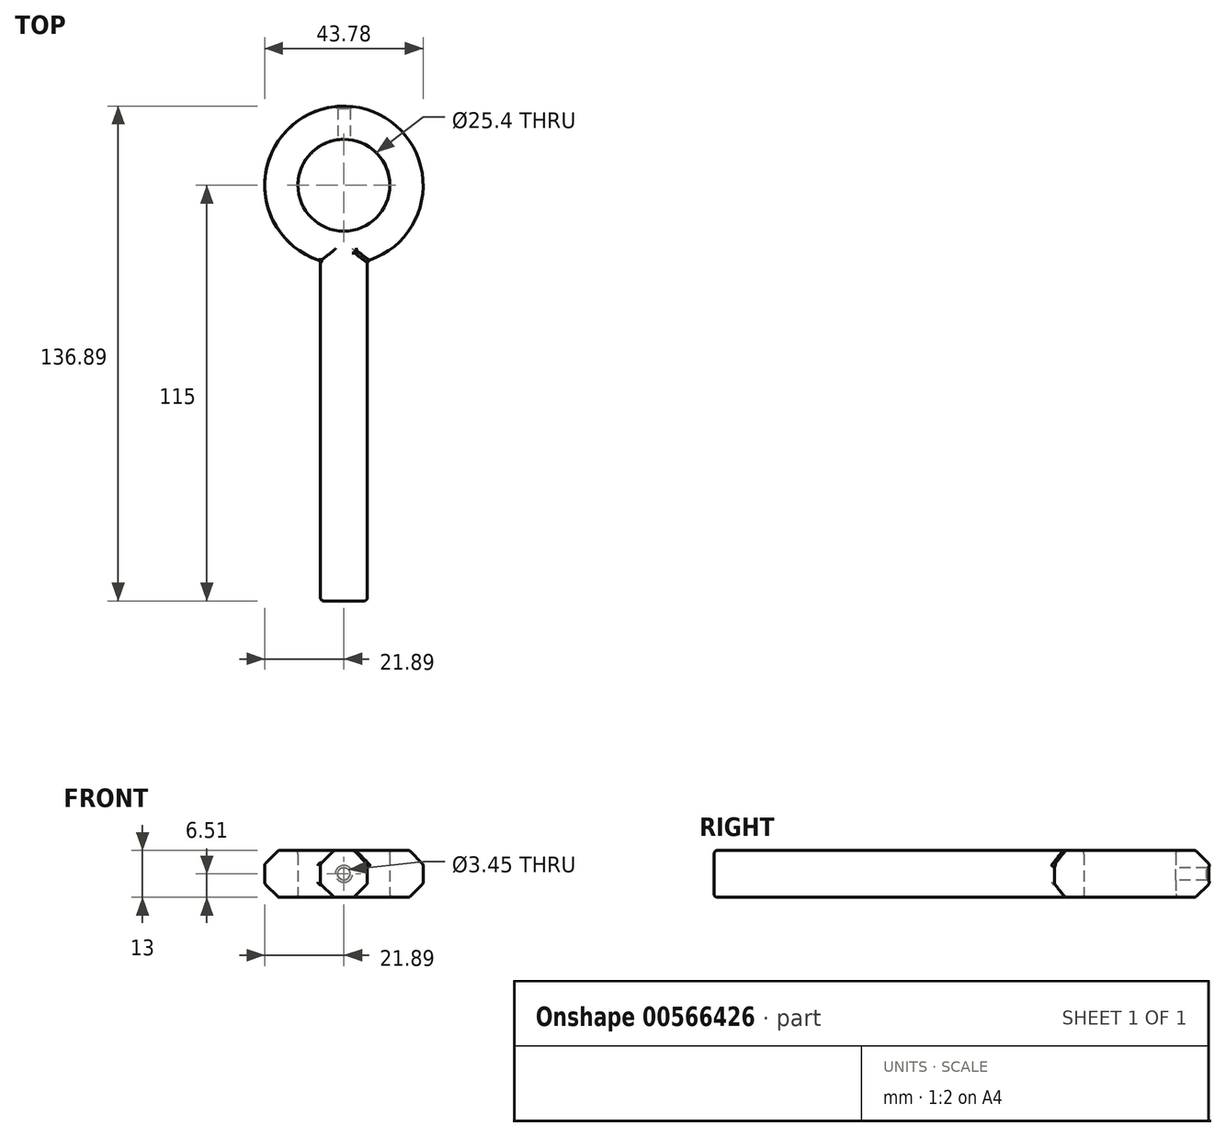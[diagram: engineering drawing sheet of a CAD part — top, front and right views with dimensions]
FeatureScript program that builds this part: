
annotation { "Feature Type Name" : "Feature", "Feature Type Description" : "" }
export const myFeature = defineFeature(function(context is Context, id is Id, definition is map)
    precondition{}
    {
        {
            var Q0;
            Q0=qCreatedBy(makeId("Right.planeOp"),FACE);
            var sketch = newSketch(context, id + "F0", { "sketchPlane" : qUnion([Q0])});
            skLineSegment(sketch, "E0", {"start": v(-12.7, 6.49) * mm, "end": v(-18.08, 6.49) * mm});
            skLineSegment(sketch, "E1", {"start": v(-18.08, 6.49) * mm, "end": v(-21.9, 2.68) * mm});
            skLineSegment(sketch, "E2", {"start": v(-21.9, 2.68) * mm, "end": v(-21.9, -2.7) * mm});
            skLineSegment(sketch, "E3", {"start": v(-21.9, -2.7) * mm, "end": v(-18.08, -6.51) * mm});
            skLineSegment(sketch, "E4", {"start": v(-18.08, -6.51) * mm, "end": v(-12.7, -6.51) * mm});
            skLineSegment(sketch, "E5", {"start": v(-12.7, 6.49) * mm, "end": v(-12.7, -6.51) * mm});
            skLineSegment(sketch, "E6", {"start": v(0, 0) * mm, "end": v(0, 10.16) * mm, "construction": true});
            skSolve(sketch);
        }
        {
            var Q0;
            Q0=makeQuery(id+"F0.imprint","IMPRINT",FACE,{"disambiguationData":[TD([[makeQuery(id+"F0.imprint","IMPRINT",EDGE,{"derivedFrom":sQuery(id+"F0.wireOp",EDGE,"E0")}),1.0]])]});
            var Q1;
            Q1=sQuery(id+"F0.wireOp",EDGE,"E6");
            revolve(context, id + "F1", {"entities" : qUnion([Q0]), "axis" : qUnion([Q1]), "revolveType" : RevolveType.FULL});
        }
        {
            var Q0;
            Q0=makeQuery(id+"F1.opRevolve","SWEPT_EDGE",EDGE,{"disambiguationData":[OSD([sQuery(id+"F0.wireOp",EDGE,"E0"),sQuery(id+"F0.wireOp",EDGE,"E5")])]});
            var Q1;
            Q1=makeQuery(id+"F1.opRevolve","SWEPT_EDGE",EDGE,{"disambiguationData":[OSD([sQuery(id+"F0.wireOp",EDGE,"E4"),sQuery(id+"F0.wireOp",EDGE,"E5")])]});
            fillet(context, id + "F2", {"entities" : qUnion([Q0, Q1]), "radius" : 1 * mm, "tangentPropagation" : true, "allowEdgeOverflow" : false});
        }
        {
            var Q0;
            Q0=makeQuery(id+"F1.opRevolve","SWEPT_EDGE",EDGE,{"disambiguationData":[OSD([sQuery(id+"F0.wireOp",EDGE,"E1"),sQuery(id+"F0.wireOp",EDGE,"E2")])]});
            var Q1;
            Q1=makeQuery(id+"F1.opRevolve","SWEPT_EDGE",EDGE,{"disambiguationData":[OSD([sQuery(id+"F0.wireOp",EDGE,"E0"),sQuery(id+"F0.wireOp",EDGE,"E1")])]});
            var Q2;
            Q2=makeQuery(id+"F1.opRevolve","SWEPT_EDGE",EDGE,{"disambiguationData":[OSD([sQuery(id+"F0.wireOp",EDGE,"E2"),sQuery(id+"F0.wireOp",EDGE,"E3")])]});
            var Q3;
            Q3=makeQuery(id+"F1.opRevolve","SWEPT_EDGE",EDGE,{"disambiguationData":[OSD([sQuery(id+"F0.wireOp",EDGE,"E3"),sQuery(id+"F0.wireOp",EDGE,"E4")])]});
            fillet(context, id + "F3", {"entities" : qUnion([Q0, Q1, Q2, Q3]), "radius" : 1 * mm, "tangentPropagation" : true, "allowEdgeOverflow" : false});
        }
        {
            var Q0;
            Q0=qCreatedBy(makeId("Front.planeOp"),FACE);
            var sketch = newSketch(context, id + "F4", { "sketchPlane" : qUnion([Q0])});
            skCircle(sketch, "E7", {"center": v(0, 0) * mm, "radius": 1.73 * mm});
            skSolve(sketch);
        }
        {
            var Q0;
            Q0 = qSketchRegion(id + "F4", true);
            extrude(context, id + "F5", {"entities" : qUnion([Q0]), "operationType" : NewBodyOperationType.REMOVE, "oppositeDirection" : true, "depth" : 25 * mm, "offsetDistance" : 25 * mm});
        }
        {
            var Q0;
            Q0=qCreatedBy(makeId("Front.planeOp"),FACE);
            var sketch = newSketch(context, id + "F6", { "sketchPlane" : qUnion([Q0])});
            skLineSegment(sketch, "E8", {"start": v(-6.5, 2.68) * mm, "end": v(-6.5, -2.7) * mm});
            skLineSegment(sketch, "E9", {"start": v(-6.5, -2.7) * mm, "end": v(-2.7, -6.51) * mm});
            skLineSegment(sketch, "E10", {"start": v(-2.7, -6.51) * mm, "end": v(2.7, -6.51) * mm});
            skLineSegment(sketch, "E11", {"start": v(2.7, -6.51) * mm, "end": v(6.5, -2.7) * mm});
            skLineSegment(sketch, "E12", {"start": v(6.5, -2.7) * mm, "end": v(6.5, 2.68) * mm});
            skLineSegment(sketch, "E13", {"start": v(6.5, 2.68) * mm, "end": v(2.7, 6.49) * mm});
            skLineSegment(sketch, "E14", {"start": v(2.7, 6.49) * mm, "end": v(-2.7, 6.49) * mm});
            skLineSegment(sketch, "E15", {"start": v(-2.7, 6.49) * mm, "end": v(-6.5, 2.68) * mm});
            skSolve(sketch);
        }
        {
            var Q0;
            Q0=makeQuery(id+"F6.imprint","IMPRINT",FACE,{"disambiguationData":[TD([[makeQuery(id+"F6.imprint","IMPRINT",EDGE,{"derivedFrom":sQuery(id+"F6.wireOp",EDGE,"E8")}),1.0]])]});
            extrude(context, id + "F7", {"entities" : qUnion([Q0]), "operationType" : NewBodyOperationType.ADD, "depth" : 115 * mm, "offsetDistance" : 25 * mm, "hasSecondDirection" : true, "secondDirectionOppositeDirection" : false, "secondDirectionDepth" : 15 * mm});
        }
        {
            var Q0;
            Q0=makeQuery(id+"F7.opExtrude","SWEPT_EDGE",EDGE,{"disambiguationData":[OSD([sQuery(id+"F6.wireOp",EDGE,"E14"),sQuery(id+"F6.wireOp",EDGE,"E15")])]});
            var Q1;
            Q1=makeQuery(id+"F7.opExtrude","SWEPT_EDGE",EDGE,{"disambiguationData":[OSD([sQuery(id+"F6.wireOp",EDGE,"E13"),sQuery(id+"F6.wireOp",EDGE,"E14")])]});
            var Q2;
            Q2=makeQuery(id+"F7.opExtrude","SWEPT_EDGE",EDGE,{"disambiguationData":[OSD([sQuery(id+"F6.wireOp",EDGE,"E8"),sQuery(id+"F6.wireOp",EDGE,"E15")])]});
            var Q3;
            Q3=makeQuery(id+"F7.opExtrude","SWEPT_FACE",FACE,{"disambiguationData":[OSD([sQuery(id+"F6.wireOp",EDGE,"E8")])]});
            var Q4;
            Q4=makeQuery(id+"F7.opExtrude","SWEPT_EDGE",EDGE,{"disambiguationData":[OSD([sQuery(id+"F6.wireOp",EDGE,"E9"),sQuery(id+"F6.wireOp",EDGE,"E10")])]});
            var Q5;
            Q5=makeQuery(id+"F7.opExtrude","SWEPT_EDGE",EDGE,{"disambiguationData":[OSD([sQuery(id+"F6.wireOp",EDGE,"E12"),sQuery(id+"F6.wireOp",EDGE,"E13")])]});
            var Q6;
            Q6=makeQuery(id+"F7.opExtrude","SWEPT_EDGE",EDGE,{"disambiguationData":[OSD([sQuery(id+"F6.wireOp",EDGE,"E11"),sQuery(id+"F6.wireOp",EDGE,"E12")])]});
            var Q7;
            Q7=makeQuery(id+"F7.opExtrude","SWEPT_EDGE",EDGE,{"disambiguationData":[OSD([sQuery(id+"F6.wireOp",EDGE,"E10"),sQuery(id+"F6.wireOp",EDGE,"E11")])]});
            var Q8;
            Q8=makeQuery(id+"F7.boolean.opBoolean","INTERSECT",EDGE,{"derivedFrom":[makeQuery(id+"F1.opRevolve","SWEPT_FACE",FACE,{"disambiguationData":[OSD([sQuery(id+"F0.wireOp",EDGE,"E1")])]}),makeQuery(id+"F7.opExtrude","SWEPT_FACE",FACE,{"disambiguationData":[OSD([sQuery(id+"F6.wireOp",EDGE,"E13")])]})]});
            var Q9;
            Q9=makeQuery(id+"F7.opExtrude","CAP_EDGE",EDGE,{"disambiguationData":[OSD([sQuery(id+"F6.wireOp",EDGE,"E15")])],"isStart":false});
            var Q10;
            Q10=makeQuery(id+"F7.opExtrude","CAP_EDGE",EDGE,{"disambiguationData":[OSD([sQuery(id+"F6.wireOp",EDGE,"E14")])],"isStart":false});
            var Q11;
            Q11=makeQuery(id+"F7.opExtrude","CAP_EDGE",EDGE,{"disambiguationData":[OSD([sQuery(id+"F6.wireOp",EDGE,"E13")])],"isStart":false});
            var Q12;
            Q12=makeQuery(id+"F7.opExtrude","CAP_EDGE",EDGE,{"disambiguationData":[OSD([sQuery(id+"F6.wireOp",EDGE,"E12")])],"isStart":false});
            var Q13;
            Q13=makeQuery(id+"F7.opExtrude","CAP_EDGE",EDGE,{"disambiguationData":[OSD([sQuery(id+"F6.wireOp",EDGE,"E11")])],"isStart":false});
            var Q14;
            Q14=makeQuery(id+"F7.opExtrude","CAP_EDGE",EDGE,{"disambiguationData":[OSD([sQuery(id+"F6.wireOp",EDGE,"E10")])],"isStart":false});
            var Q15;
            Q15=makeQuery(id+"F7.opExtrude","CAP_EDGE",EDGE,{"disambiguationData":[OSD([sQuery(id+"F6.wireOp",EDGE,"E9")])],"isStart":false});
            fillet(context, id + "F8", {"entities" : qUnion([Q0, Q1, Q2, Q3, Q4, Q5, Q6, Q7, Q8, Q9, Q10, Q11, Q12, Q13, Q14, Q15]), "radius" : 1 * mm, "tangentPropagation" : true, "allowEdgeOverflow" : false});
        }
        {
            var Q0;
            Q0=makeQuery(id+"F5.boolean.opBoolean","INTERSECT",EDGE,{"derivedFrom":[makeQuery(id+"F1.opRevolve","SWEPT_FACE",FACE,{"disambiguationData":[OSD([sQuery(id+"F0.wireOp",EDGE,"E2")])]}),makeQuery(id+"F5.opExtrude","SWEPT_FACE",FACE,{"disambiguationData":[OSD([sQuery(id+"F4.wireOp",EDGE,"E7")])]})]});
            chamfer(context, id + "F9", {"entities" : qUnion([Q0]), "width" : .6 * mm, "tangentPropagation" : true});
        }
    });
